# Revit family: Cocoon Media Space (Full Configuration)
name_source: partatom
category: Generic Models
revit_build: Autodesk Revit 2018 (Build: 20181011_1500(x64)
units: mm (PartAtom-declared; Revit-internal decimal feet)

## family parameters
Always vertical = Yes
Can host rebar = No
Cut with Voids When Loaded = No
Part Type = Normal
Room Calculation Point = No
Round Connector Dimension = Use Diameter
Shared = No
Work Plane-Based = No

## types (1)
- Cocoon Media Space (Full Configuration)
    Back Fabric = Cocoon Media Space Back Fabric
    High Frame = Cocoon Media Space High Frame
    High Surface = Cocoon Media Space High Surface
    Seat Fabric = Cocoon Media Space Seat Fabric
    TV Screen = Cocoon Media Space TV Screen Generic
    Table Edgeband = Cocoon Media Space Edgeband
    Table Surface = Cocoon Media Space Surface
    Wall Surface = Cocoon Media Space Wall Surface

## geometry (parser evidence)
native form markers: Sweep x38
no freeform markers — native parametric forms only
